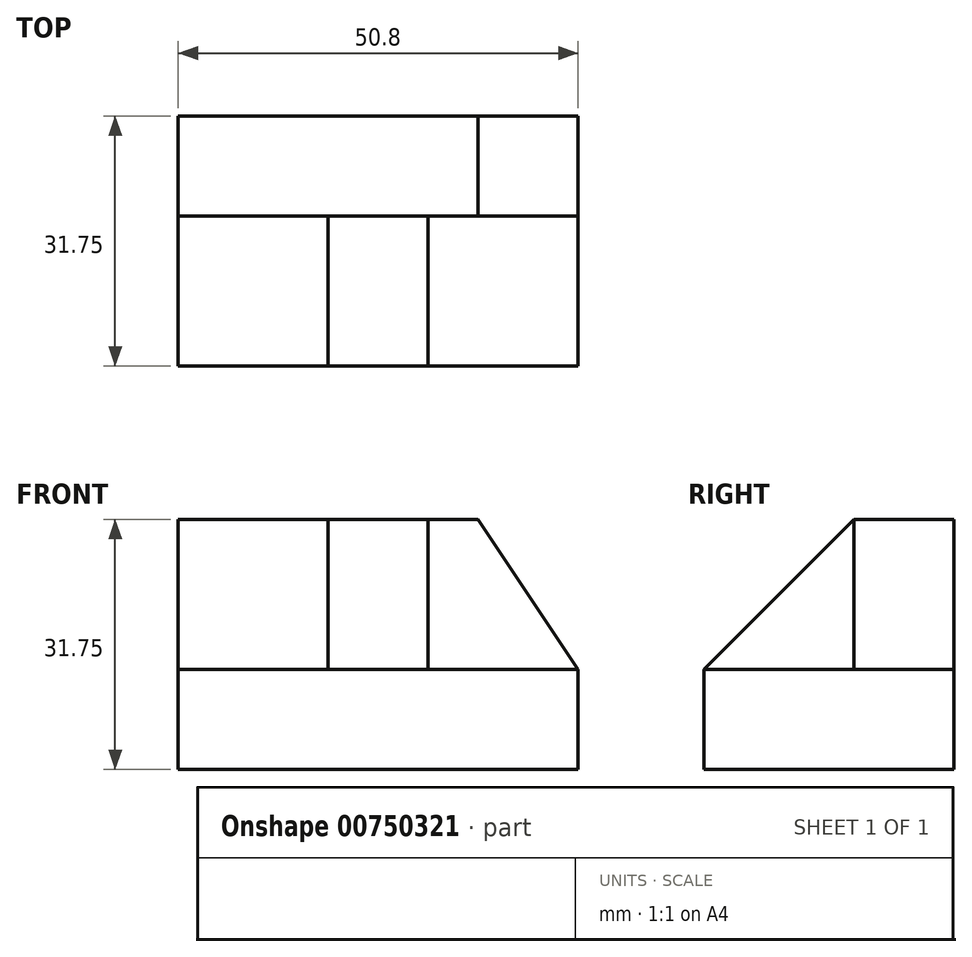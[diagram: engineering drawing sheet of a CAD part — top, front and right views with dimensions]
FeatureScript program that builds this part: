
annotation { "Feature Type Name" : "Feature", "Feature Type Description" : "" }
export const myFeature = defineFeature(function(context is Context, id is Id, definition is map)
    precondition{}
    {
        {
            var Q0;
            Q0=qCreatedBy(makeId("Front.planeOp"),FACE);
            var sketch = newSketch(context, id + "F0", { "sketchPlane" : qUnion([Q0])});
            skLineSegment(sketch, "E0", {"start": v(0, 0) * mm, "end": v(50.8, 0) * mm});
            skLineSegment(sketch, "E1", {"start": v(50.8, 0) * mm, "end": v(50.8, 31.75) * mm});
            skLineSegment(sketch, "E2", {"start": v(50.8, 31.75) * mm, "end": v(0, 31.75) * mm});
            skLineSegment(sketch, "E3", {"start": v(0, 31.75) * mm, "end": v(0, 0) * mm});
            skSolve(sketch);
        }
        {
            var Q0;
            Q0 = qSketchRegion(id + "F0", true);
            extrude(context, id + "F1", {"entities" : qUnion([Q0]), "depth" : 31.75 * mm, "offsetDistance" : 25.4 * mm});
        }
        {
            var Q0;
            Q0=makeQuery(id+"F1.opExtrude","SWEPT_FACE",FACE,{"disambiguationData":[OSD([sQuery(id+"F0.wireOp",EDGE,"E2")])]});
            var sketch = newSketch(context, id + "F2", { "sketchPlane" : qUnion([Q0])});
            skLineSegment(sketch, "E4", {"start": v(0, -12.7) * mm, "end": v(19.05, -12.7) * mm});
            skLineSegment(sketch, "E5", {"start": v(19.05, -12.7) * mm, "end": v(19.05, -31.75) * mm});
            skLineSegment(sketch, "E6", {"start": v(19.05, -31.75) * mm, "end": v(0, -31.75) * mm});
            skLineSegment(sketch, "E7", {"start": v(0, -31.75) * mm, "end": v(0, -12.7) * mm});
            skLineSegment(sketch, "E8", {"start": v(31.75, -31.75) * mm, "end": v(31.75, -12.7) * mm});
            skLineSegment(sketch, "E9", {"start": v(31.75, -12.7) * mm, "end": v(50.8, -12.7) * mm});
            skLineSegment(sketch, "E10", {"start": v(50.8, -12.7) * mm, "end": v(50.8, -31.75) * mm});
            skLineSegment(sketch, "E11", {"start": v(50.8, -31.75) * mm, "end": v(31.75, -31.75) * mm});
            skSolve(sketch);
        }
        {
            var Q0;
            Q0 = qSketchRegion(id + "F2", true);
            extrude(context, id + "F3", {"entities" : qUnion([Q0]), "operationType" : NewBodyOperationType.REMOVE, "oppositeDirection" : true, "depth" : 19.05 * mm, "offsetDistance" : 25.4 * mm});
        }
        {
            var Q0;
            Q0=makeQuery(id+"F3.boolean.opBoolean","COPY",FACE,{"derivedFrom":makeQuery(id+"F3.opExtrude","SWEPT_FACE",FACE,{"disambiguationData":[OSD([sQuery(id+"F2.wireOp",EDGE,"E8")])]})});
            var sketch = newSketch(context, id + "F4", { "sketchPlane" : qUnion([Q0])});
            skLineSegment(sketch, "E12", {"start": v(-12.7, 31.75) * mm, "end": v(-31.75, 12.7) * mm});
            skLineSegment(sketch, "E13", {"start": v(-31.75, 12.7) * mm, "end": v(-31.75, 31.75) * mm});
            skLineSegment(sketch, "E14", {"start": v(-31.75, 31.75) * mm, "end": v(-12.7, 31.75) * mm});
            skSolve(sketch);
        }
        {
            var Q0;
            Q0 = qSketchRegion(id + "F4", true);
            extrude(context, id + "F5", {"entities" : qUnion([Q0]), "operationType" : NewBodyOperationType.REMOVE, "oppositeDirection" : true, "depth" : 25.4 * mm, "offsetDistance" : 25.4 * mm});
        }
        {
            var Q0;
            Q0=makeQuery(id+"F3.boolean.opBoolean","COPY",FACE,{"derivedFrom":makeQuery(id+"F3.opExtrude","SWEPT_FACE",FACE,{"disambiguationData":[OSD([sQuery(id+"F2.wireOp",EDGE,"E9")])]})});
            var sketch = newSketch(context, id + "F6", { "sketchPlane" : qUnion([Q0])});
            skLineSegment(sketch, "E15", {"start": v(38.1, 31.75) * mm, "end": v(50.8, 12.7) * mm});
            skLineSegment(sketch, "E16", {"start": v(50.8, 12.7) * mm, "end": v(50.8, 31.75) * mm});
            skLineSegment(sketch, "E17", {"start": v(50.8, 31.75) * mm, "end": v(38.1, 31.75) * mm});
            skSolve(sketch);
        }
        {
            var Q0;
            Q0 = qSketchRegion(id + "F6", true);
            extrude(context, id + "F7", {"entities" : qUnion([Q0]), "operationType" : NewBodyOperationType.REMOVE, "oppositeDirection" : true, "depth" : 25.4 * mm, "offsetDistance" : 25.4 * mm});
        }
    });
